# Revit family: EKF_EE_ПанелиВертикальныеДляСекционированияTrivia_AVERES
name_source: partatom
category: Электрооборудование
units: mm (PartAtom-declared; Revit-internal decimal feet)

## family parameters
Всегда вертикально = Нет
На основе рабочей плоскости = Да
Общий = Да
При загрузке вырезать с полостями = Нет
Размер круглого соединителя = Использовать диаметр
Тип детали = Силовой щит
Точка расчета площади = Нет

## types (2) — shared parameters
ADSK_Единица измерения = шт.
ADSK_Завод-изготовитель = EKF
ADSK_Количество = 1
ADSK_Материал = RAL 7035_Сталь
ADSK_Размер_Глубина = 17.5 мм
ADSK_Размер_Ширина = 215 мм
Глубина = 400 мм
Изготовитель = EKF
Отметка по умолчанию = 1219.2 мм
Серия номенклатуры = Averes
Степень защиты IP = -
ТВ = EKF_2_TRIVIA_AVERES
Тип установки = -
Тип_Панели = Вл_Панели вертикальные для секционирования_1
zero-valued in all types: ADSK_Масса

## per-type parameters (varying)
| type | ADSK_Код изделия | ADSK_Размер_Высота | Тип |
| Панели вертикальные для секционирования В1700 Г200 мм EKF AVERES | PCV172 | 1683 мм | 712 мм |
| Панели вертикальные для секционирования В1900 Г200 мм EKF AVERES | PCV192 | 1917 мм | 716 мм |

note: column(s) folded — value = type name in every type: ADSK_Марка, ADSK_Наименование, ADSK_Обозначение
